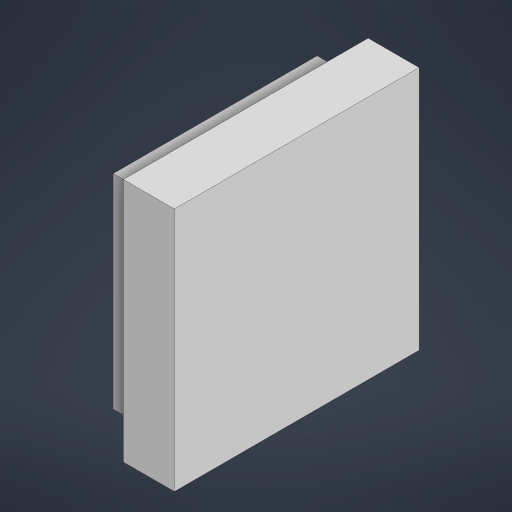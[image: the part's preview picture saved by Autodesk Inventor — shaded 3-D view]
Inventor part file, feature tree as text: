
AUTODESK INVENTOR PART (.ipt)
format: ipt  version: 2024.1 (Build 281209000, 209)  size: 154,112 bytes
history: native  units: mm
features: extrude x2, sketch x2
ambient origin geometry x8: Origin, YZ Plane, XZ Plane, XY Plane, X Axis, Y Axis, Z Axis, Center Point
bodies: Solid1 (feature_tree)
feature tree (4):
  extrude  "Extrusion1"  Depth=12.0mm
  extrude  "Extrusion2"  Depth=10.0mm
  sketch  "Sketch1"  dims[d0=12.0mm d1=12.0mm]
  sketch  "Sketch2"  dims[d2=2.5mm d3=0.0mm d4=10.0mm d5=10.0mm d6=1.5mm d7=0.0mm]
